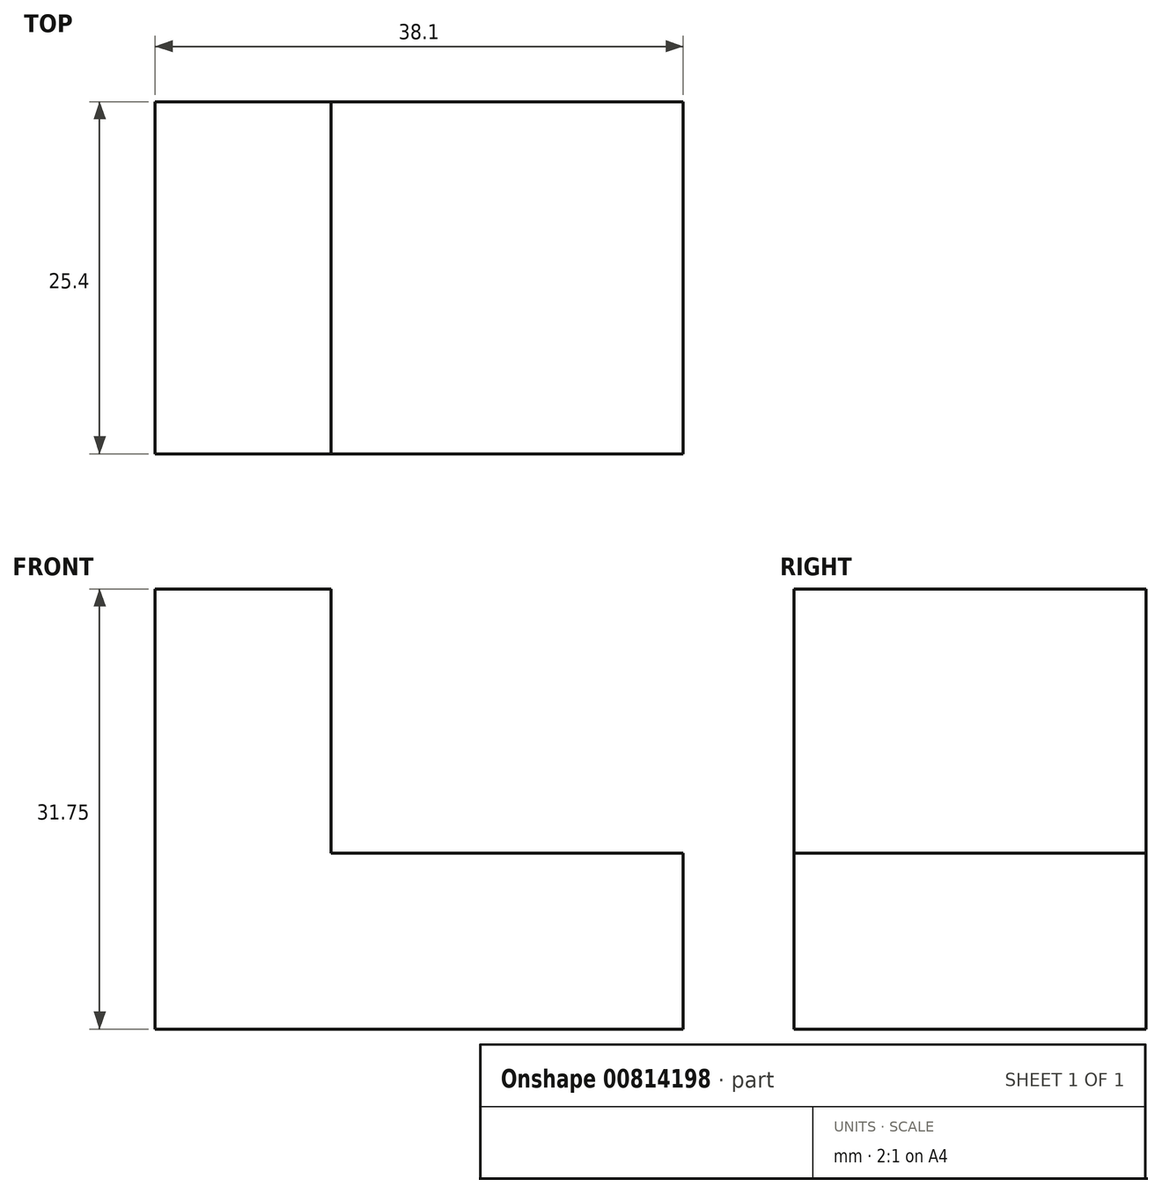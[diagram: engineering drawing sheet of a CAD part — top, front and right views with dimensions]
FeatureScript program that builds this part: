
annotation { "Feature Type Name" : "Feature", "Feature Type Description" : "" }
export const myFeature = defineFeature(function(context is Context, id is Id, definition is map)
    precondition{}
    {
        {
            var Q0;
            Q0=qCreatedBy(makeId("Front.planeOp"),FACE);
            var sketch = newSketch(context, id + "F0", { "sketchPlane" : qUnion([Q0])});
            skLineSegment(sketch, "E0.bottom", {"start": v(0, 0) * mm, "end": v(38.1, 0) * mm});
            skLineSegment(sketch, "E0.top", {"start": v(0, 31.75) * mm, "end": v(38.1, 31.75) * mm});
            skLineSegment(sketch, "E0.left", {"start": v(0, 0) * mm, "end": v(0, 31.75) * mm});
            skLineSegment(sketch, "E0.right", {"start": v(38.1, 0) * mm, "end": v(38.1, 31.75) * mm});
            skSolve(sketch);
        }
        {
            var Q0;
            Q0=makeQuery(id+"F0.imprint","IMPRINT",FACE,{"disambiguationData":[TD([[makeQuery(id+"F0.imprint","IMPRINT",EDGE,{"derivedFrom":sQuery(id+"F0.wireOp",EDGE,"E0.bottom")}),1.0]])]});
            extrude(context, id + "F1", {"entities" : qUnion([Q0]), "depth" : 25.4 * mm, "offsetDistance" : 25.4 * mm});
        }
        {
            var Q0;
            Q0=makeQuery(id+"F1.opExtrude","CAP_FACE",FACE,{"disambiguationData":[OSD([sQuery(id+"F0.wireOp",EDGE,"E0.bottom"),sQuery(id+"F0.wireOp",EDGE,"E0.top"),sQuery(id+"F0.wireOp",EDGE,"E0.left"),sQuery(id+"F0.wireOp",EDGE,"E0.right")])],"isStart":false});
            var sketch = newSketch(context, id + "F2", { "sketchPlane" : qUnion([Q0])});
            skLineSegment(sketch, "E1", {"start": v(0, 31.75) * mm, "end": v(12.7, 31.75) * mm});
            skLineSegment(sketch, "E2", {"start": v(12.7, 31.75) * mm, "end": v(12.7, 12.7) * mm});
            skLineSegment(sketch, "E3", {"start": v(12.7, 12.7) * mm, "end": v(38.1, 12.7) * mm});
            skSolve(sketch);
        }
        {
            var Q0;
            Q0 = qSketchRegion(id + "F2", true);
            var Q1;
            {var subQ0=sQuery(id+"F2.wireOp",EDGE,"E2");Q1=makeQuery(id+"F2.imprint","IMPRINT",FACE,{"disambiguationData":[TD([[makeQuery(id+"F2.imprint","IMPRINT",EDGE,{"derivedFrom":subQ0}),1.0]])]});}
            extrude(context, id + "F3", {"entities" : qUnion([Q0, Q1]), "operationType" : NewBodyOperationType.REMOVE, "oppositeDirection" : true, "depth" : 25.4 * mm, "offsetDistance" : 25.4 * mm});
        }
    });
